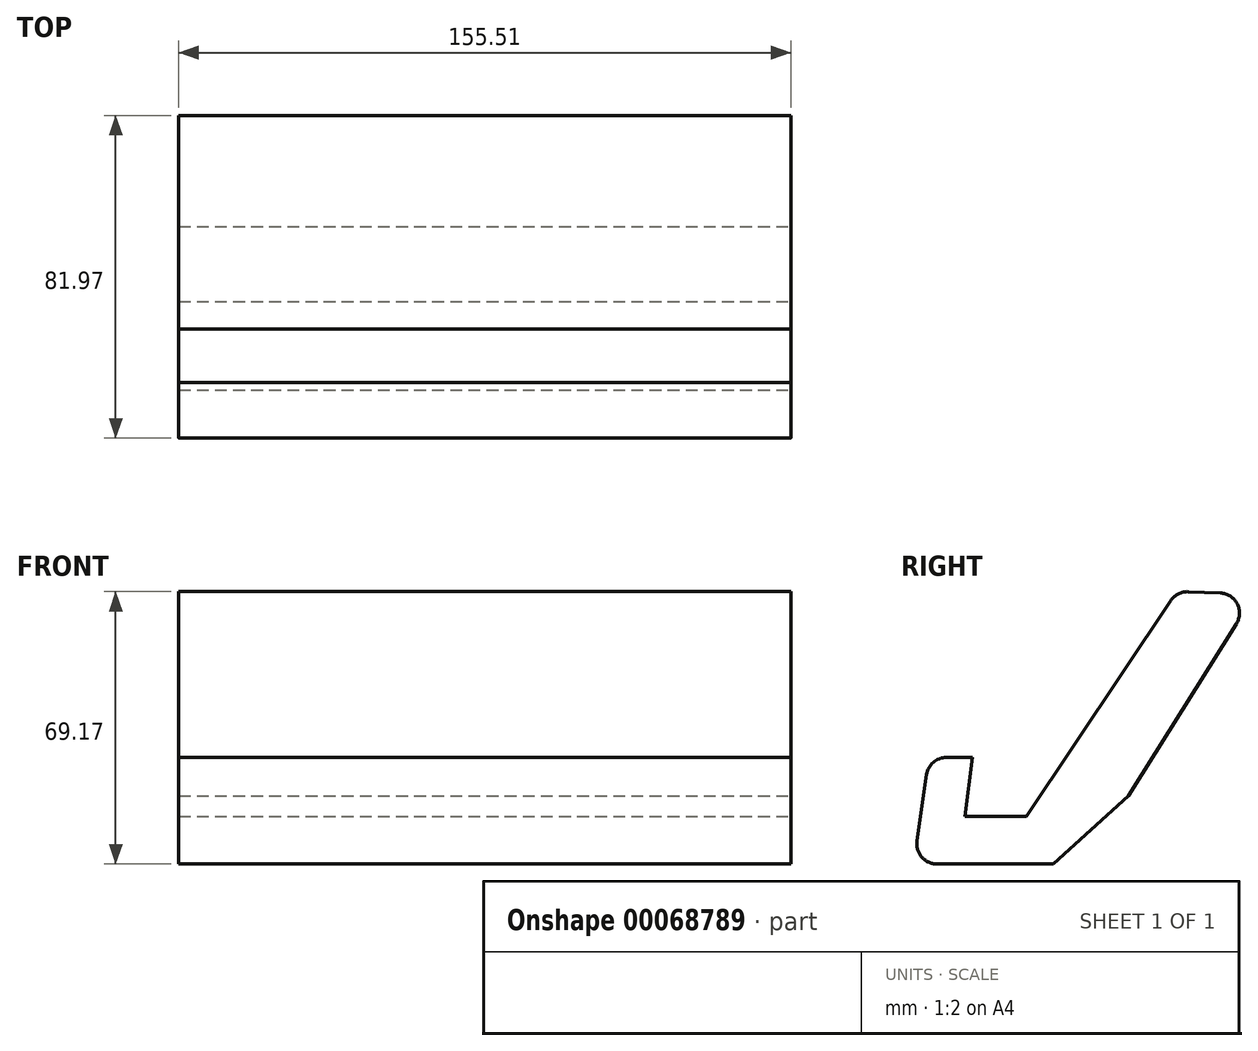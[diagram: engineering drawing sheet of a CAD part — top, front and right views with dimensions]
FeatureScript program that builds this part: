
annotation { "Feature Type Name" : "Feature", "Feature Type Description" : "" }
export const myFeature = defineFeature(function(context is Context, id is Id, definition is map)
    precondition{}
    {
        {
            var Q0;
            Q0=qCreatedBy(makeId("Right.planeOp"),FACE);
            var sketch = newSketch(context, id + "F0", { "sketchPlane" : qUnion([Q0])});
            skLineSegment(sketch, "E0", {"start": v(28.47, 44.28) * mm, "end": v(-9.85, -12.88) * mm});
            skLineSegment(sketch, "E1", {"start": v(-9.85, -12.88) * mm, "end": v(-25.44, -12.88) * mm});
            skLineSegment(sketch, "E2", {"start": v(-25.44, -12.88) * mm, "end": v(-23.5, 2.06) * mm});
            skLineSegment(sketch, "E3", {"start": v(-23.5, 2.06) * mm, "end": v(-34.54, 2.06) * mm});
            skLineSegment(sketch, "E4", {"start": v(-34.54, 2.06) * mm, "end": v(-38.44, -25) * mm});
            skLineSegment(sketch, "E5", {"start": v(-38.44, -25) * mm, "end": v(-2.92, -25) * mm});
            skLineSegment(sketch, "E6", {"start": v(-2.92, -25) * mm, "end": v(16.13, -7.69) * mm});
            skLineSegment(sketch, "E7", {"start": v(16.13, -7.69) * mm, "end": v(48.18, 43.42) * mm});
            skLineSegment(sketch, "E8", {"start": v(48.18, 43.42) * mm, "end": v(28.47, 44.28) * mm});
            skSolve(sketch);
        }
        {
            var Q0;
            Q0 = qSketchRegion(id + "F0", true);
            extrude(context, id + "F1", {"entities" : qUnion([Q0]), "oppositeDirection" : true, "depth" : 155.5 * mm});
        }
        {
            var Q0;
            Q0=makeQuery(id+"F1.opExtrude","SWEPT_EDGE",EDGE,{"disambiguationData":[OSD([sQuery(id+"F0.wireOp",EDGE,"E0"),sQuery(id+"F0.wireOp",EDGE,"E8")])]});
            var Q1;
            Q1=makeQuery(id+"F1.opExtrude","SWEPT_EDGE",EDGE,{"disambiguationData":[OSD([sQuery(id+"F0.wireOp",EDGE,"E7"),sQuery(id+"F0.wireOp",EDGE,"E8")])]});
            var Q2;
            Q2=makeQuery(id+"F1.opExtrude","SWEPT_EDGE",EDGE,{"disambiguationData":[OSD([sQuery(id+"F0.wireOp",EDGE,"E3"),sQuery(id+"F0.wireOp",EDGE,"E4")])]});
            var Q3;
            Q3=makeQuery(id+"F1.opExtrude","SWEPT_EDGE",EDGE,{"disambiguationData":[OSD([sQuery(id+"F0.wireOp",EDGE,"E4"),sQuery(id+"F0.wireOp",EDGE,"E5")])]});
            fillet(context, id + "F2", {"entities" : qUnion([Q0, Q1, Q2, Q3]), "radius" : 5.08 * mm, "tangentPropagation" : true, "allowEdgeOverflow" : false});
        }
    });
